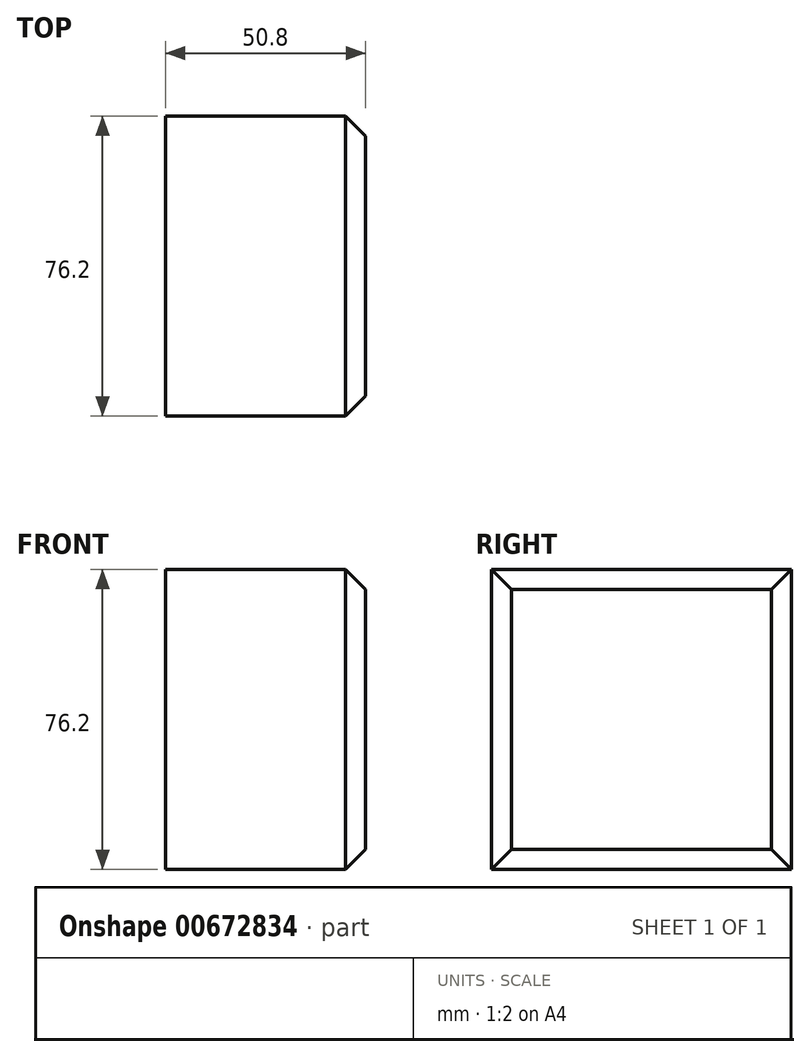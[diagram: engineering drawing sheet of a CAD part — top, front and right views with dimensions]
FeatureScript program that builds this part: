
annotation { "Feature Type Name" : "Feature", "Feature Type Description" : "" }
export const myFeature = defineFeature(function(context is Context, id is Id, definition is map)
    precondition{}
    {
        {
            var Q0;
            Q0=qCreatedBy(makeId("Right.planeOp"),FACE);
            var sketch = newSketch(context, id + "F0", { "sketchPlane" : qUnion([Q0])});
            skLineSegment(sketch, "E0.bottom", {"start": v(0, 0) * mm, "end": v(76.2, 0) * mm});
            skLineSegment(sketch, "E0.top", {"start": v(0, -76.2) * mm, "end": v(76.2, -76.2) * mm});
            skLineSegment(sketch, "E0.left", {"start": v(0, 0) * mm, "end": v(0, -76.2) * mm});
            skLineSegment(sketch, "E0.right", {"start": v(76.2, 0) * mm, "end": v(76.2, -76.2) * mm});
            skSolve(sketch);
        }
        {
            var Q0;
            Q0 = qSketchRegion(id + "F0", true);
            extrude(context, id + "F1", {"entities" : qUnion([Q0]), "depth" : 50.8 * mm, "offsetDistance" : 25.4 * mm});
        }
        {
            var Q0;
            Q0=makeQuery(id+"F1.opExtrude","CAP_EDGE",EDGE,{"disambiguationData":[OSD([sQuery(id+"F0.wireOp",EDGE,"E0.bottom")])],"isStart":false});
            var Q1;
            Q1=makeQuery(id+"F1.opExtrude","CAP_EDGE",EDGE,{"disambiguationData":[OSD([sQuery(id+"F0.wireOp",EDGE,"E0.left")])],"isStart":false});
            var Q2;
            Q2=makeQuery(id+"F1.opExtrude","CAP_EDGE",EDGE,{"disambiguationData":[OSD([sQuery(id+"F0.wireOp",EDGE,"E0.right")])],"isStart":false});
            var Q3;
            Q3=makeQuery(id+"F1.opExtrude","CAP_EDGE",EDGE,{"disambiguationData":[OSD([sQuery(id+"F0.wireOp",EDGE,"E0.top")])],"isStart":false});
            chamfer(context, id + "F2", {"entities" : qUnion([Q0, Q1, Q2, Q3]), "width" : 5.08 * mm, "tangentPropagation" : true});
        }
    });
